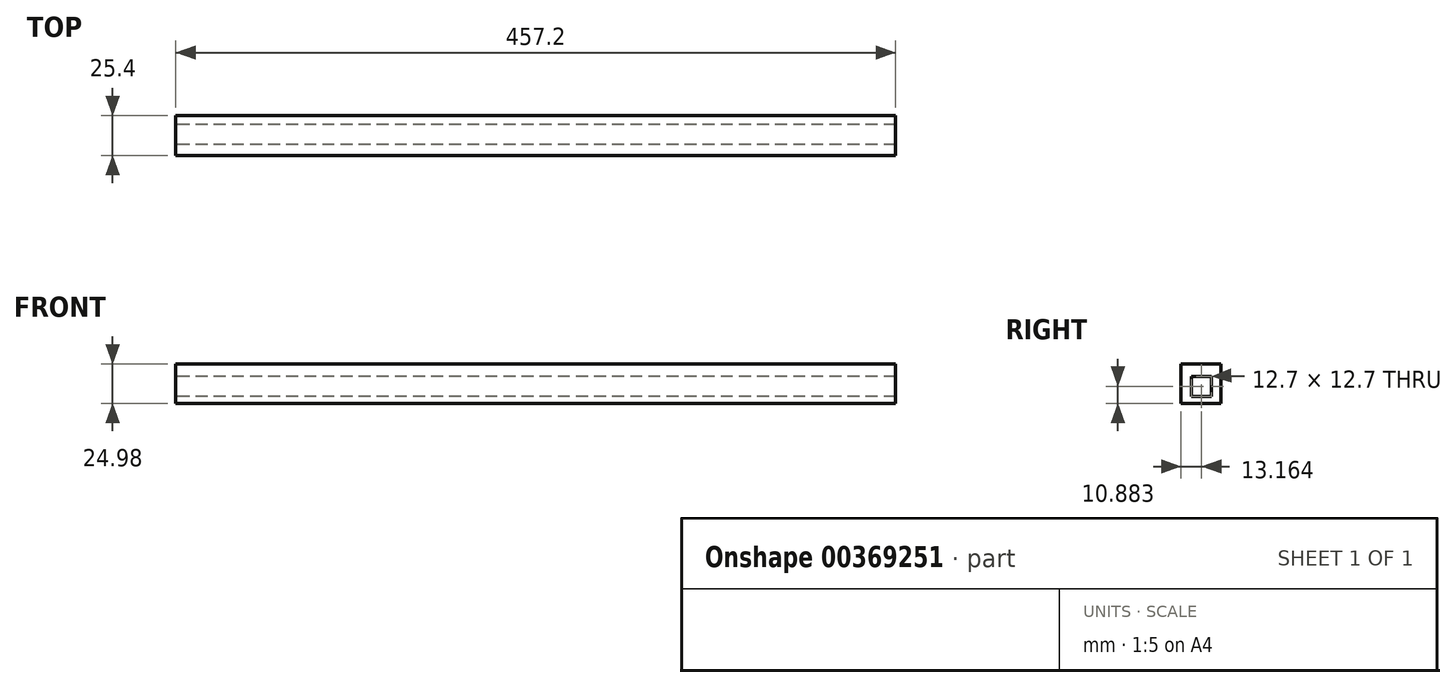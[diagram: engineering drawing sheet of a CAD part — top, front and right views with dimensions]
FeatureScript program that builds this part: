
annotation { "Feature Type Name" : "Feature", "Feature Type Description" : "" }
export const myFeature = defineFeature(function(context is Context, id is Id, definition is map)
    precondition{}
    {
        {
            var Q0;
            Q0=qCreatedBy(makeId("Right.planeOp"),FACE);
            var sketch = newSketch(context, id + "F0", { "sketchPlane" : qUnion([Q0])});
            skLineSegment(sketch, "E0.bottom", {"start": v(-56.19, 12.23) * mm, "end": v(-30.79, 12.23) * mm});
            skLineSegment(sketch, "E0.top", {"start": v(-56.19, -12.75) * mm, "end": v(-30.79, -12.75) * mm});
            skLineSegment(sketch, "E0.left", {"start": v(-56.19, 12.23) * mm, "end": v(-56.19, -12.75) * mm});
            skLineSegment(sketch, "E0.right", {"start": v(-30.79, 12.23) * mm, "end": v(-30.79, -12.75) * mm});
            skLineSegment(sketch, "E1.bottom", {"start": v(-49.38, 4.48) * mm, "end": v(-36.68, 4.48) * mm});
            skLineSegment(sketch, "E1.top", {"start": v(-49.38, -8.22) * mm, "end": v(-36.68, -8.22) * mm});
            skLineSegment(sketch, "E1.left", {"start": v(-49.38, 4.48) * mm, "end": v(-49.38, -8.22) * mm});
            skLineSegment(sketch, "E1.right", {"start": v(-36.68, 4.48) * mm, "end": v(-36.68, -8.22) * mm});
            skSolve(sketch);
        }
        {
            var Q0;
            Q0 = qSketchRegion(id + "F0", true);
            extrude(context, id + "F1", {"entities" : qUnion([Q0]), "depth" : 457.2 * mm});
        }
    });
